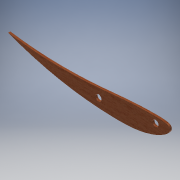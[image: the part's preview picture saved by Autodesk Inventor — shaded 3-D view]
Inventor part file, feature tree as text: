
AUTODESK INVENTOR PART (.ipt)
format: ipt  version: 2018 (Build 220112000, 112)  size: 142,848 bytes
history: native  units: mm
features: extrude x2, sketch x2, other x1, projected_geometry x1
ambient origin geometry x8: Origin, YZ Plane, XZ Plane, XY Plane, X Axis, Y Axis, Z Axis, Center Point
bodies: Body1 (feature_tree)
feature tree (6):
  extrude  "押し出し1"  Depth=4.0mm TaperAngle=0.0deg
  extrude  "押し出し2"  Depth=20.0mm
  other  "厚み1"
  sketch  "スケッチ1"
  projected_geometry  "投影ループ1"
  sketch  "スケッチ2"
